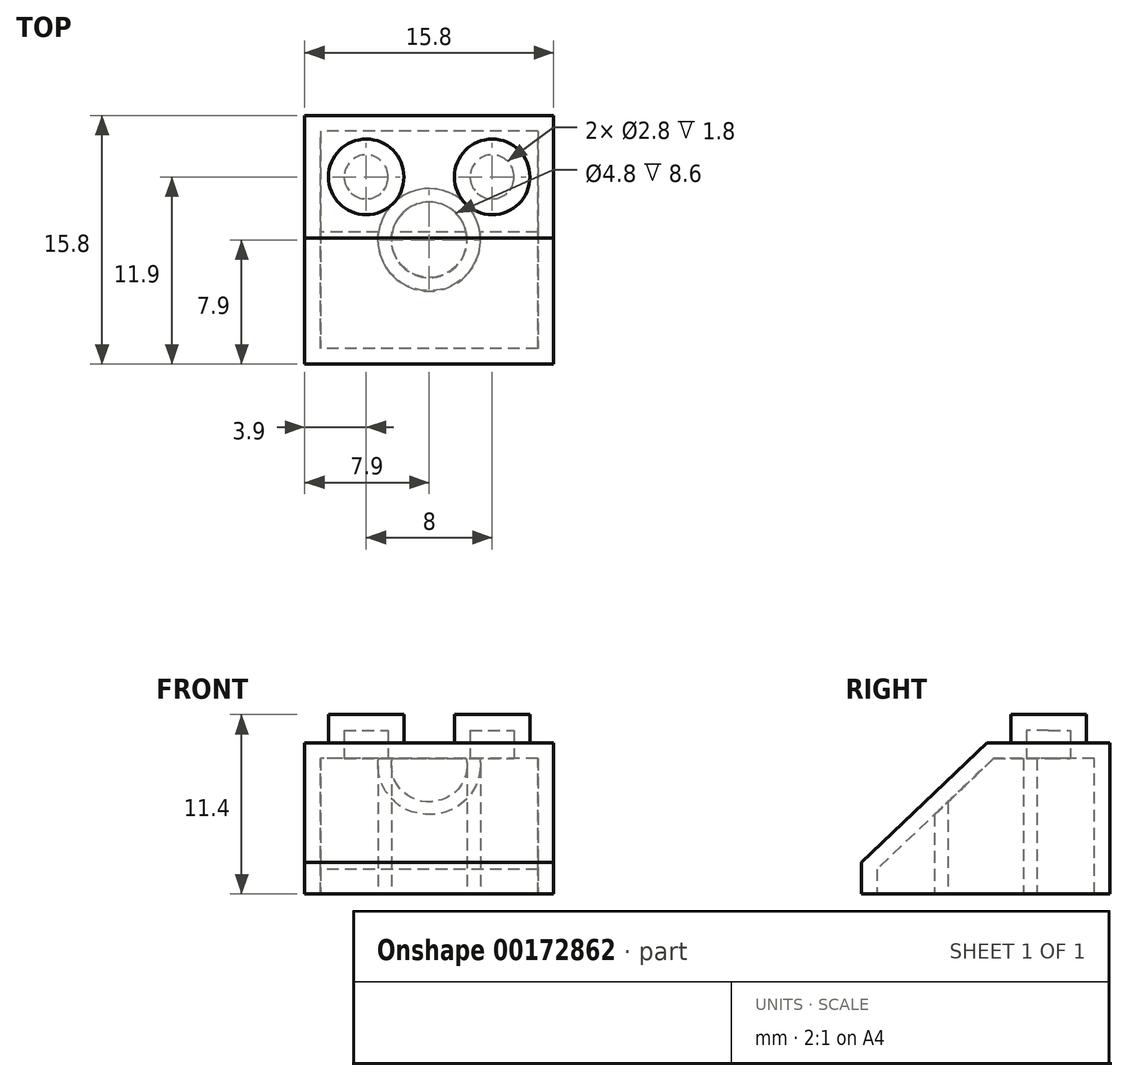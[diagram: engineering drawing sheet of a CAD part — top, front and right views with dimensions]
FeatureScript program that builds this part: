
annotation { "Feature Type Name" : "Feature", "Feature Type Description" : "" }
export const myFeature = defineFeature(function(context is Context, id is Id, definition is map)
    precondition{}
    {
        {
            var Q0;
            Q0=qCreatedBy(makeId("Right.planeOp"),FACE);
            var sketch = newSketch(context, id + "F0", { "sketchPlane" : qUnion([Q0])});
            skLineSegment(sketch, "E0", {"start": v(0, 0) * mm, "end": v(0, 9.6) * mm});
            skLineSegment(sketch, "E1", {"start": v(0, 9.6) * mm, "end": v(-7.8, 9.6) * mm});
            skLineSegment(sketch, "E2", {"start": v(-7.8, 9.6) * mm, "end": v(-15.8, 2) * mm});
            skLineSegment(sketch, "E3", {"start": v(-15.8, 2) * mm, "end": v(-15.8, 0) * mm});
            skLineSegment(sketch, "E4", {"start": v(-15.8, 0) * mm, "end": v(0, 0) * mm});
            skSolve(sketch);
        }
        {
            var Q0;
            Q0 = qSketchRegion(id + "F0", true);
            extrude(context, id + "F1", {"entities" : qUnion([Q0]), "endBound" : BoundingType.SYMMETRIC, "depth" : 15.8 * mm});
        }
        {
            var Q0;
            Q0=makeQuery(id+"F1.opExtrude","SWEPT_FACE",FACE,{"disambiguationData":[OSD([sQuery(id+"F0.wireOp",EDGE,"E1")])]});
            var sketch = newSketch(context, id + "F2", { "sketchPlane" : qUnion([Q0])});
            skCircle(sketch, "E5", {"center": v(-4, -3.9) * mm, "radius": 2.4 * mm});
            skCircle(sketch, "E6", {"center": v(4, -3.9) * mm, "radius": 2.4 * mm});
            skLineSegment(sketch, "E7", {"start": v(-4, -3.9) * mm, "end": v(4, -3.9) * mm, "construction": true});
            skPoint(sketch, "E8", {"position": v(0, -3.9) * mm});
            skPoint(sketch, "E9", {"position": v(7.9, -3.9) * mm});
            skSolve(sketch);
        }
        {
            var Q0;
            Q0 = qSketchRegion(id + "F2", true);
            extrude(context, id + "F3", {"entities" : qUnion([Q0]), "operationType" : NewBodyOperationType.ADD, "depth" : 1.8 * mm});
        }
        {
            var Q0;
            Q0=makeQuery(id+"F1.opExtrude","SWEPT_FACE",FACE,{"disambiguationData":[OSD([sQuery(id+"F0.wireOp",EDGE,"E4")])]});
            shell(context, id + "F4", {"entities" : qUnion([Q0]), "thickness" : 1 * mm});
        }
        {
            var Q0;
            Q0=makeQuery(id+"F1.opExtrude","SWEPT_FACE",FACE,{"disambiguationData":[OSD([sQuery(id+"F0.wireOp",EDGE,"E4")])]});
            var sketch = newSketch(context, id + "F5", { "sketchPlane" : qUnion([Q0])});
            skPoint(sketch, "E10", {"position": v(6.9, 7.9) * mm});
            skCircle(sketch, "E11", {"center": v(0, 7.9) * mm, "radius": 2.4 * mm});
            skCircle(sketch, "E12", {"center": v(0, 7.9) * mm, "radius": 3.25 * mm});
            skSolve(sketch);
        }
        {
            var Q0;
            Q0 = qSketchRegion(id + "F5", true);
            extrude(context, id + "F6", {"entities" : qUnion([Q0]), "operationType" : NewBodyOperationType.ADD, "endBound" : BoundingType.UP_TO_NEXT, "oppositeDirection" : true, "depth" : 25 * mm});
        }
    });
